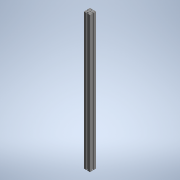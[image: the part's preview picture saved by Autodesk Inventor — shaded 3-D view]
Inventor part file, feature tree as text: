
AUTODESK INVENTOR PART (.ipt)
format: ipt  version: 2022 (Build 260153000, 153)  size: 224,256 bytes
history: native  units: mm (DEFAULTED — no unit token found)
features: other x21, sketch x2, extrude x1, hole x1
ambient origin geometry x8: Origin, YZ Plane, XZ Plane, XY Plane, X Axis, Y Axis, Z Axis, Center Point
bodies: Solid1 (feature_tree)
feature tree (25):
  extrude  "Extrusion1"  TaperAngle=0.0deg  [1 undecoded]
  hole  "Hole1"  [1 undecoded]
  other  "C1_XY"
  other  "C1_YZ"
  other  "C1_ZX"
  other  "C1_X"
  other  "C1_Y"
  other  "C1_Z"
  other  "C1_Center"
  other  "to_frame_cap1_XY"
  other  "to_frame_cap1_YZ"
  other  "to_frame_cap1_ZX"
  other  "to_frame_cap1_X"
  other  "to_frame_cap1_Y"
  other  "to_frame_cap1_Z"
  other  "to_frame_cap1_Center"
  other  "to_frame_cap2_XY"
  other  "to_frame_cap2_YZ"
  other  "to_frame_cap2_ZX"
  other  "to_frame_cap2_X"
  other  "to_frame_cap2_Y"
  other  "to_frame_cap2_Z"
  other  "to_frame_cap2_Center"
  sketch  "Sketch_60"  dims[d2=10.5mm d3=6.0mm d4=4.0mm d5=2.0mm d6=90.0deg d7=1000.0mm d8=0.0mm d9=0.0mm d10=0.0mm d11=0.0mm d12=152.4mm d13=0.872665mm d14=152.4mm d15=0.872665mm]
  sketch  "Sketch2"  dims[d0=1320.8mm d1=0.0mm]
note: 2 required parameter values undecoded (feature->parameter linkage not recoverable at this tier; creation-order binding heuristic only, values carry confidence <= 0.55)
